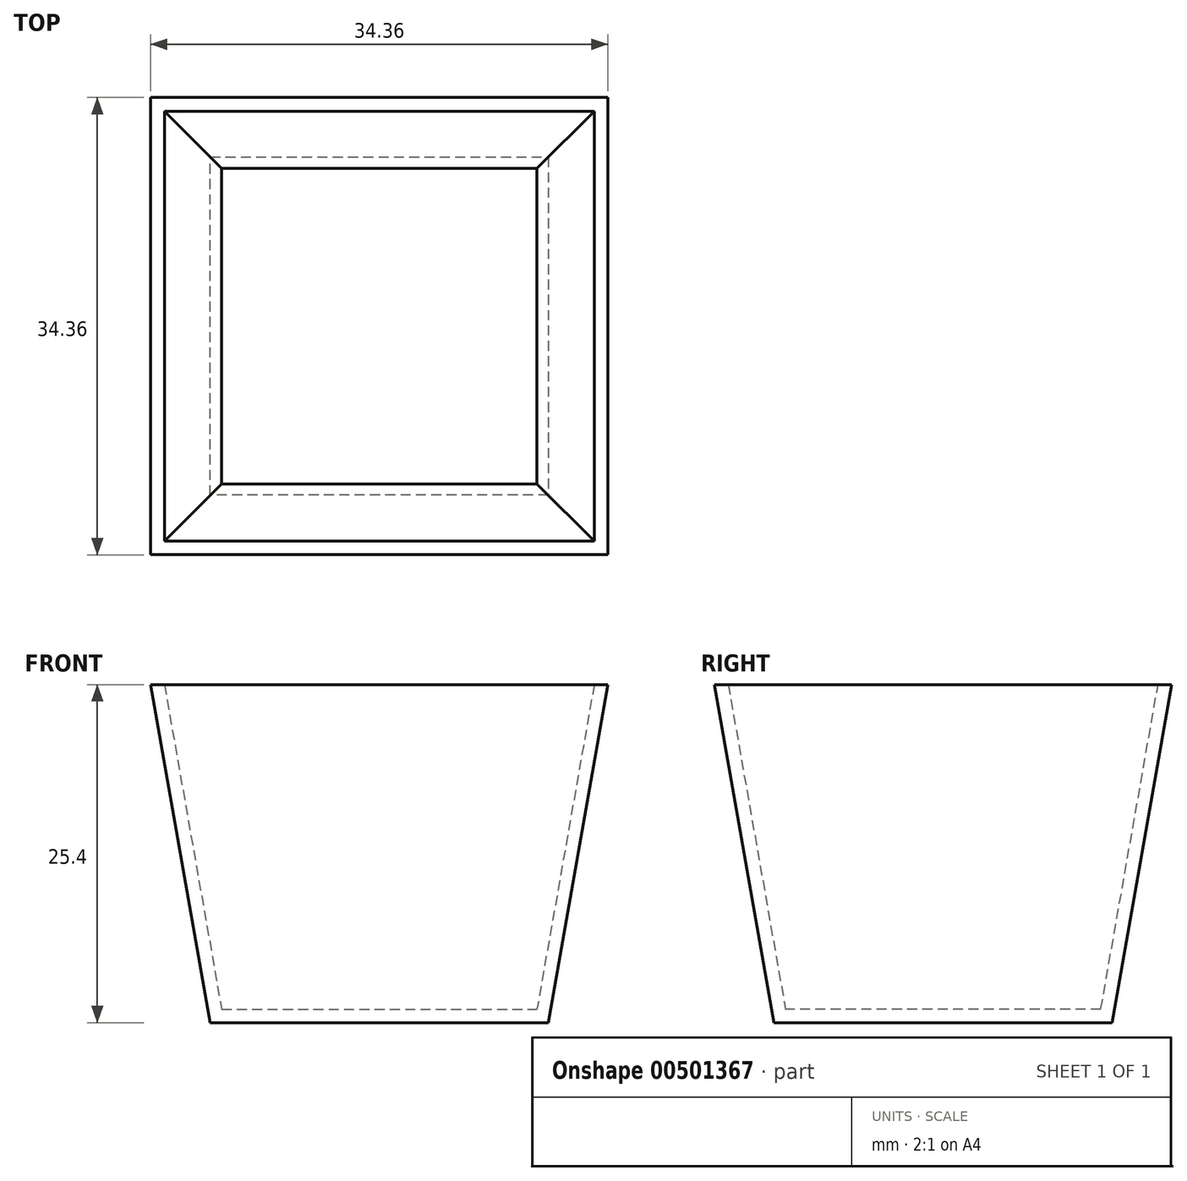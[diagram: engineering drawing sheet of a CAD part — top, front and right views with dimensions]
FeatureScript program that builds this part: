
annotation { "Feature Type Name" : "Feature", "Feature Type Description" : "" }
export const myFeature = defineFeature(function(context is Context, id is Id, definition is map)
    precondition{}
    {
        {
            var Q0;
            Q0=qCreatedBy(makeId("Top.planeOp"),FACE);
            var sketch = newSketch(context, id + "F0", { "sketchPlane" : qUnion([Q0])});
            skLineSegment(sketch, "E0.bottom", {"start": v(12.7, 12.7) * mm, "end": v(-12.7, 12.7) * mm});
            skLineSegment(sketch, "E0.top", {"start": v(12.7, -12.7) * mm, "end": v(-12.7, -12.7) * mm});
            skLineSegment(sketch, "E0.left", {"start": v(12.7, 12.7) * mm, "end": v(12.7, -12.7) * mm});
            skLineSegment(sketch, "E0.right", {"start": v(-12.7, 12.7) * mm, "end": v(-12.7, -12.7) * mm});
            skPoint(sketch, "E0.middle", {"position": v(0, 0) * mm});
            skSolve(sketch);
        }
        {
            var Q0;
            Q0 = qSketchRegion(id + "F0", true);
            extrude(context, id + "F1", {"entities" : qUnion([Q0]), "depth" : 25.4 * mm, "offsetDistance" : 25.4 * mm, "hasDraft" : true, "draftAngle" : 10 * degree});
        }
        {
            var Q0;
            Q0=makeQuery(id+"F1.opExtrude","CAP_FACE",FACE,{"disambiguationData":[OSD([sQuery(id+"F0.wireOp",EDGE,"E0.bottom"),sQuery(id+"F0.wireOp",EDGE,"E0.top"),sQuery(id+"F0.wireOp",EDGE,"E0.left"),sQuery(id+"F0.wireOp",EDGE,"E0.right")])],"isStart":false});
            shell(context, id + "F2", {"entities" : qUnion([Q0]), "thickness" : 1.02 * mm});
        }
    });
